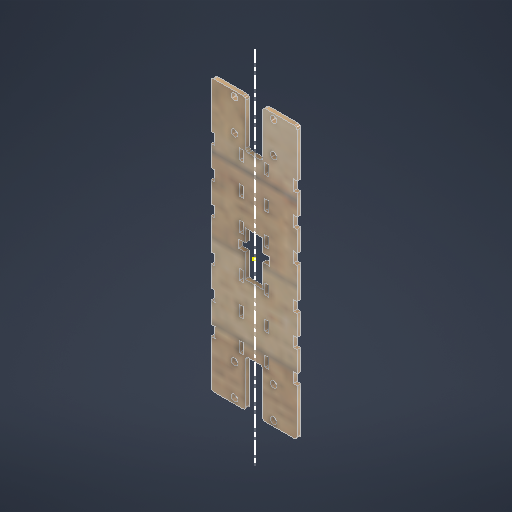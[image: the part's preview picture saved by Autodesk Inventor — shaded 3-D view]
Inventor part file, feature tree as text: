
AUTODESK INVENTOR PART (.ipt)
format: ipt  version: 2025.3 (Build 293356030, 356C)  size: 437,760 bytes
history: native  units: mm
features: other x2, sketch x2, extrude x1
ambient origin geometry x8: Origin, YZ Plane, XZ Plane, XY Plane, X Axis, Y Axis, Z Axis, Center Point
bodies: Body1 (feature_tree)
feature tree (5):
  other  "實體1"
  extrude  "擠出1"  Depth=66.0mm
  sketch  "草圖2"
  sketch  "草圖1"
  other  "草圖 - 矩形陣列1"
